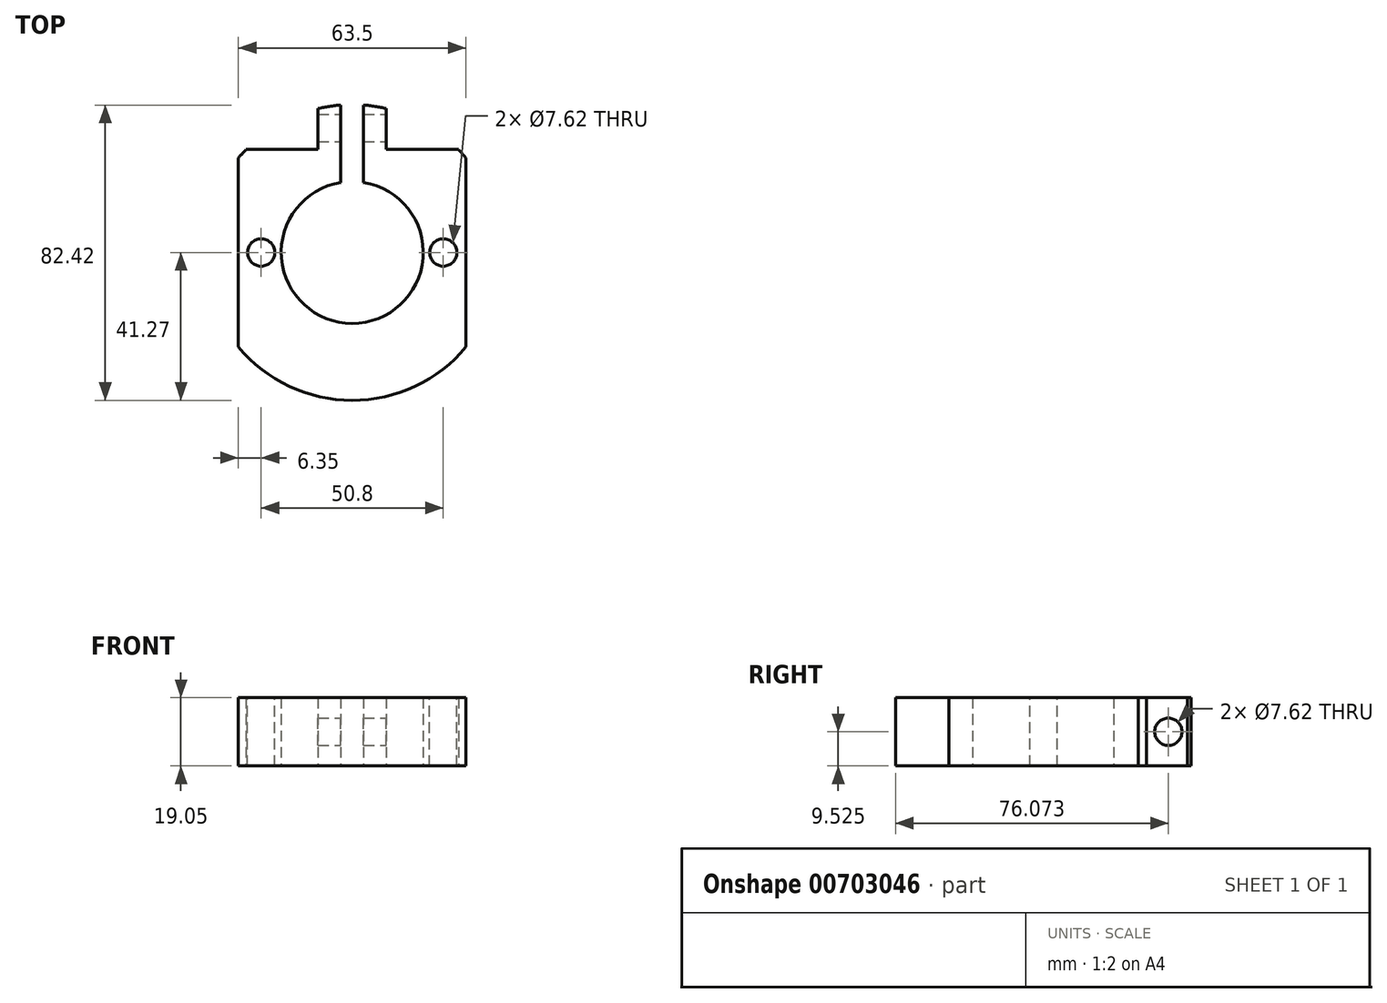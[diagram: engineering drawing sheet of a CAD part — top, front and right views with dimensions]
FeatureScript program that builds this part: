
annotation { "Feature Type Name" : "Feature", "Feature Type Description" : "" }
export const myFeature = defineFeature(function(context is Context, id is Id, definition is map)
    precondition{}
    {
        {
            var Q0;
            Q0=qCreatedBy(makeId("Top.planeOp"),FACE);
            var sketch = newSketch(context, id + "F0", { "sketchPlane" : qUnion([Q0])});
            skLineSegment(sketch, "E0", {"start": v(-3.18, 41.15) * mm, "end": v(-3.17, 19.56) * mm});
            skLineSegment(sketch, "E1", {"start": v(3.17, 41.15) * mm, "end": v(3.18, 19.56) * mm});
            skLineSegment(sketch, "E2", {"start": v(9.52, 40.16) * mm, "end": v(9.52, 28.73) * mm});
            skArc(sketch, "E3", {"start": v(-3.17, 19.56) * mm, "mid": v(0, -19.81) * mm, "end": v(3.18, 19.56) * mm});
            skLineSegment(sketch, "E4", {"start": v(-9.53, 40.16) * mm, "end": v(-9.53, 40.16) * mm});
            skArc(sketch, "E5", {"start": v(-3.17, 41.15) * mm, "mid": v(-6.37, 40.78) * mm, "end": v(-9.53, 40.16) * mm});
            skLineSegment(sketch, "E6", {"start": v(-29.63, 28.73) * mm, "end": v(-9.52, 28.73) * mm});
            skLineSegment(sketch, "E7", {"start": v(9.52, 28.73) * mm, "end": v(29.63, 28.73) * mm});
            skArc(sketch, "E8", {"start": v(9.52, 40.16) * mm, "mid": v(6.37, 40.78) * mm, "end": v(3.18, 41.15) * mm});
            skLineSegment(sketch, "E9", {"start": v(-9.53, 40.16) * mm, "end": v(-9.52, 28.73) * mm});
            skArc(sketch, "E10", {"start": v(-29.63, 28.73) * mm, "mid": v(-30.71, 27.57) * mm, "end": v(-31.75, 26.37) * mm});
            skLineSegment(sketch, "E11", {"start": v(-31.75, 26.37) * mm, "end": v(-31.75, -26.37) * mm});
            skArc(sketch, "E12", {"start": v(-31.75, -26.37) * mm, "mid": v(0, -41.28) * mm, "end": v(31.75, -26.37) * mm});
            skLineSegment(sketch, "E13", {"start": v(31.75, 26.37) * mm, "end": v(31.75, -26.37) * mm});
            skArc(sketch, "E14", {"start": v(29.63, 28.73) * mm, "mid": v(30.71, 27.57) * mm, "end": v(31.75, 26.37) * mm});
            skSolve(sketch);
        }
        {
            var Q0;
            Q0=makeQuery(id+"F0.imprint","IMPRINT",FACE,{"disambiguationData":[TD([[makeQuery(id+"F0.imprint","IMPRINT",EDGE,{"derivedFrom":sQuery(id+"F0.wireOp",EDGE,"E0")}),-1.0]])]});
            extrude(context, id + "F1", {"entities" : qUnion([Q0]), "depth" : 19.05 * mm, "offsetDistance" : 25.4 * mm});
        }
        {
            var Q0;
            Q0=makeQuery(id+"F1.opExtrude","CAP_FACE",FACE,{"disambiguationData":[OSD([sQuery(id+"F0.wireOp",EDGE,"E0"),sQuery(id+"F0.wireOp",EDGE,"E1"),sQuery(id+"F0.wireOp",EDGE,"OZVWY9np-lNkr-bDu5-xFDM-HjF8tuwzFg92"),sQuery(id+"F0.wireOp",EDGE,"E2"),sQuery(id+"F0.wireOp",EDGE,"0JBFX1wH-cFMN-VFwh-cvOb-Yx0uVQFAUVXI"),sQuery(id+"F0.wireOp",EDGE,"c797b7f7-037d-4193-ae7b-2a6c80d229eb1"),sQuery(id+"F0.wireOp",EDGE,"E3"),sQuery(id+"F0.wireOp",EDGE,"E4"),sQuery(id+"F0.wireOp",EDGE,"19527d09-b5f4-43a2-8a17-8468eb9c3a8a"),sQuery(id+"F0.wireOp",EDGE,"10e46e8e-dcbe-41ea-82a5-2c7609f11023")])],"isStart":false});
            var sketch = newSketch(context, id + "F2", { "sketchPlane" : qUnion([Q0])});
            skCircle(sketch, "E15", {"center": v(-25.4, 0) * mm, "radius": 3.81 * mm});
            skCircle(sketch, "E16", {"center": v(25.4, 0) * mm, "radius": 3.81 * mm});
            skSolve(sketch);
        }
        {
            var Q0;
            Q0=makeQuery(id+"F2.imprint","IMPRINT",FACE,{"disambiguationData":[TD([[makeQuery(id+"F2.imprint","IMPRINT",EDGE,{"derivedFrom":sQuery(id+"F2.wireOp",EDGE,"E16")}),1.0]])]});
            var Q1;
            Q1=makeQuery(id+"F2.imprint","IMPRINT",FACE,{"disambiguationData":[TD([[makeQuery(id+"F2.imprint","IMPRINT",EDGE,{"derivedFrom":sQuery(id+"F2.wireOp",EDGE,"E15")}),1.0]])]});
            var Q2;
            Q2=sQuery(id+"F2.wireOp",EDGE,"E15");
            var Q3;
            Q3=sQuery(id+"F2.wireOp",EDGE,"E16");
            extrude(context, id + "F3", {"entities" : qUnion([Q0, Q1]), "operationType" : NewBodyOperationType.REMOVE, "surfaceEntities" : qUnion([Q2, Q3]), "oppositeDirection" : true, "depth" : 25.4 * mm, "offsetDistance" : 25.4 * mm});
        }
        {
            var Q0;
            Q0=makeQuery(id+"F1.opExtrude","SWEPT_FACE",FACE,{"disambiguationData":[OSD([sQuery(id+"F0.wireOp",EDGE,"E2")])]});
            var sketch = newSketch(context, id + "F4", { "sketchPlane" : qUnion([Q0])});
            skCircle(sketch, "E17", {"center": v(34.8, 9.53) * mm, "radius": 3.81 * mm});
            skSolve(sketch);
        }
        {
            var Q0;
            Q0=makeQuery(id+"F4.imprint","IMPRINT",FACE,{"disambiguationData":[TD([[makeQuery(id+"F4.imprint","IMPRINT",EDGE,{"derivedFrom":sQuery(id+"F4.wireOp",EDGE,"E17")}),1.0]])]});
            extrude(context, id + "F5", {"entities" : qUnion([Q0]), "operationType" : NewBodyOperationType.REMOVE, "oppositeDirection" : true, "depth" : 25.4 * mm, "offsetDistance" : 25.4 * mm});
        }
    });
